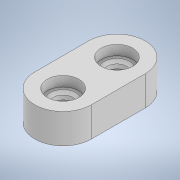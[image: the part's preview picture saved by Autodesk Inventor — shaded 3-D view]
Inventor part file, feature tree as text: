
AUTODESK INVENTOR PART (.ipt)
format: ipt  version: 2021 (Build 250183000, 183)  size: 142,336 bytes
history: native  units: mm
features: extrude x2, sketch x2, plane x1, chamfer x1
ambient origin geometry x8: Origin, YZ Plane, XZ Plane, XY Plane, X Axis, Y Axis, Z Axis, Center Point
bodies: Solid1 (feature_tree)
feature tree (6):
  extrude  "Extrusion1"  Depth=22.4mm
  plane  "Work Plane1"
  extrude  "Extrusion2"  Depth=38.0mm
  chamfer  "Chamfer1"  Distance=40.0mm
  sketch  "Sketch1"  dims[d0=22.4mm d1=22.4mm]
  sketch  "Sketch2"  dims[d2=0.0mm d3=38.0mm d4=40.0mm d5=40.0mm d6=21.0mm d7=0.0mm d8=-7.0mm d9=14.0mm d10=14.0mm d11=7.0mm d12=0.0mm d13=2.0mm d14=2.0mm d15=45.0deg]
